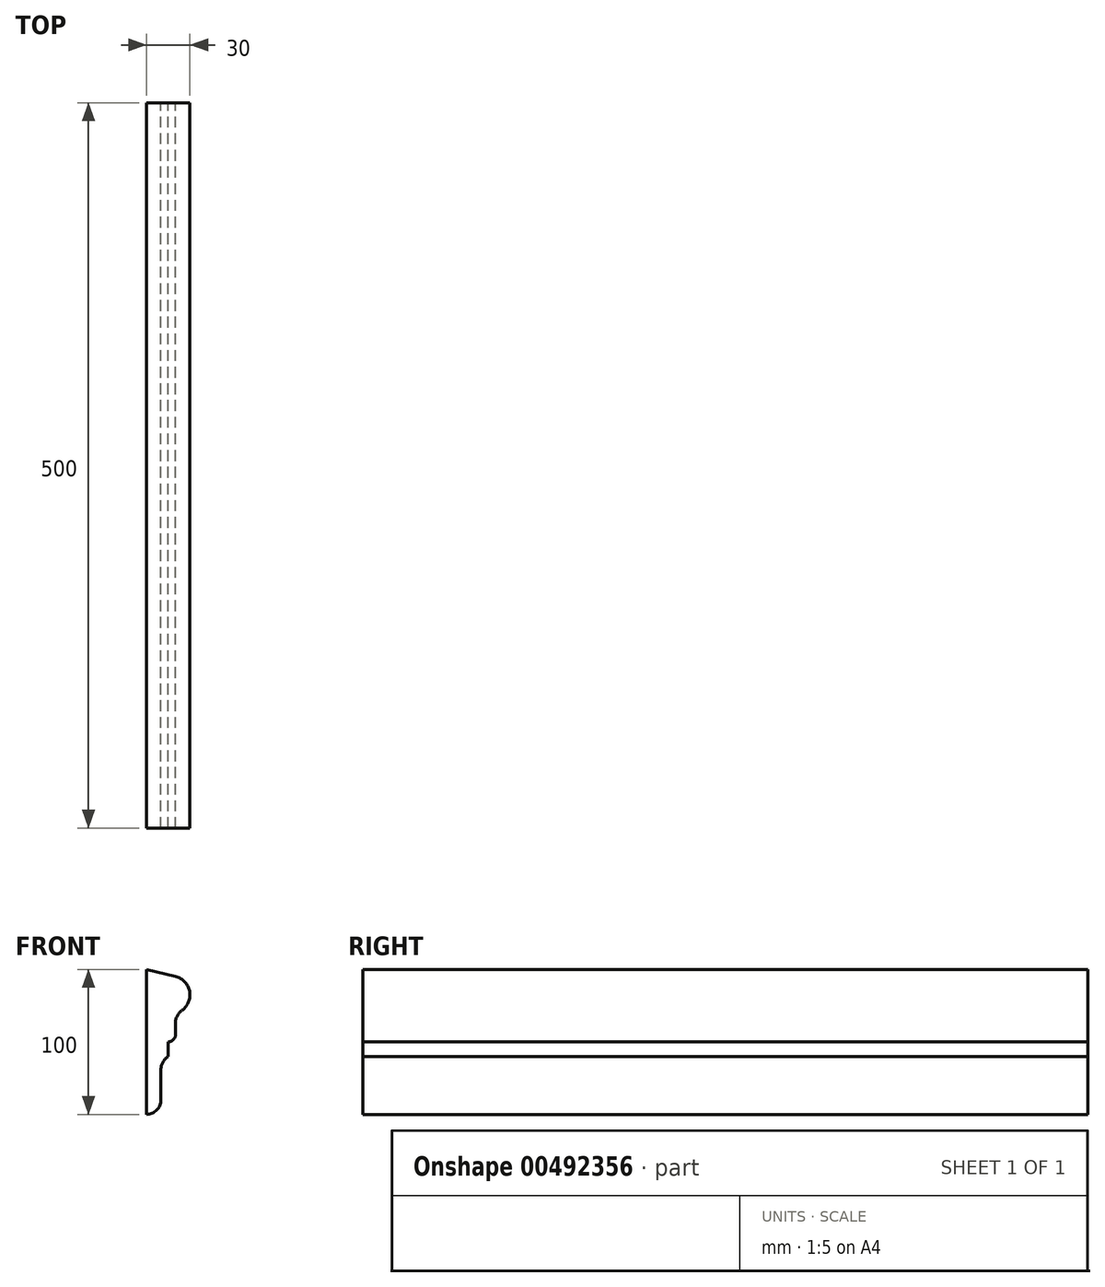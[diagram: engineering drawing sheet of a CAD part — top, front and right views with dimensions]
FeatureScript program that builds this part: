
annotation { "Feature Type Name" : "Feature", "Feature Type Description" : "" }
export const myFeature = defineFeature(function(context is Context, id is Id, definition is map)
    precondition{}
    {
        {
            var Q0;
            Q0=qCreatedBy(makeId("Front.planeOp"),FACE);
            var sketch = newSketch(context, id + "F0", { "sketchPlane" : qUnion([Q0])});
            skLineSegment(sketch, "E0", {"start": v(0, 0) * mm, "end": v(0, 100) * mm});
            skLineSegment(sketch, "E1", {"start": v(0, 100) * mm, "end": v(20.13, 95) * mm});
            skArc(sketch, "E2", {"start": v(0, 0) * mm, "mid": v(7.07, 2.93) * mm, "end": v(10, 10) * mm});
            skLineSegment(sketch, "E3", {"start": v(10, 10) * mm, "end": v(10, 30.78) * mm});
            skArc(sketch, "E4", {"start": v(15, 40) * mm, "mid": v(11.33, 36.02) * mm, "end": v(10, 30.78) * mm});
            skLineSegment(sketch, "E5", {"start": v(15, 40) * mm, "end": v(15, 50) * mm});
            skArc(sketch, "E6", {"start": v(15, 50) * mm, "mid": v(18.54, 51.46) * mm, "end": v(20, 55) * mm});
            skLineSegment(sketch, "E7", {"start": v(20, 55) * mm, "end": v(20, 62.89) * mm});
            skArc(sketch, "E8", {"start": v(24.58, 71.82) * mm, "mid": v(21.21, 67.91) * mm, "end": v(20, 62.89) * mm});
            skArc(sketch, "E9", {"start": v(24.58, 71.82) * mm, "mid": v(29.77, 84.83) * mm, "end": v(20.13, 95) * mm});
            skLineSegment(sketch, "E10", {"start": v(17, 82.38) * mm, "end": v(30, 82.38) * mm, "construction": true});
            skSolve(sketch);
        }
        {
            var Q0;
            Q0 = qSketchRegion(id + "F0", true);
            extrude(context, id + "F1", {"entities" : qUnion([Q0]), "depth" : 500 * mm});
        }
    });
